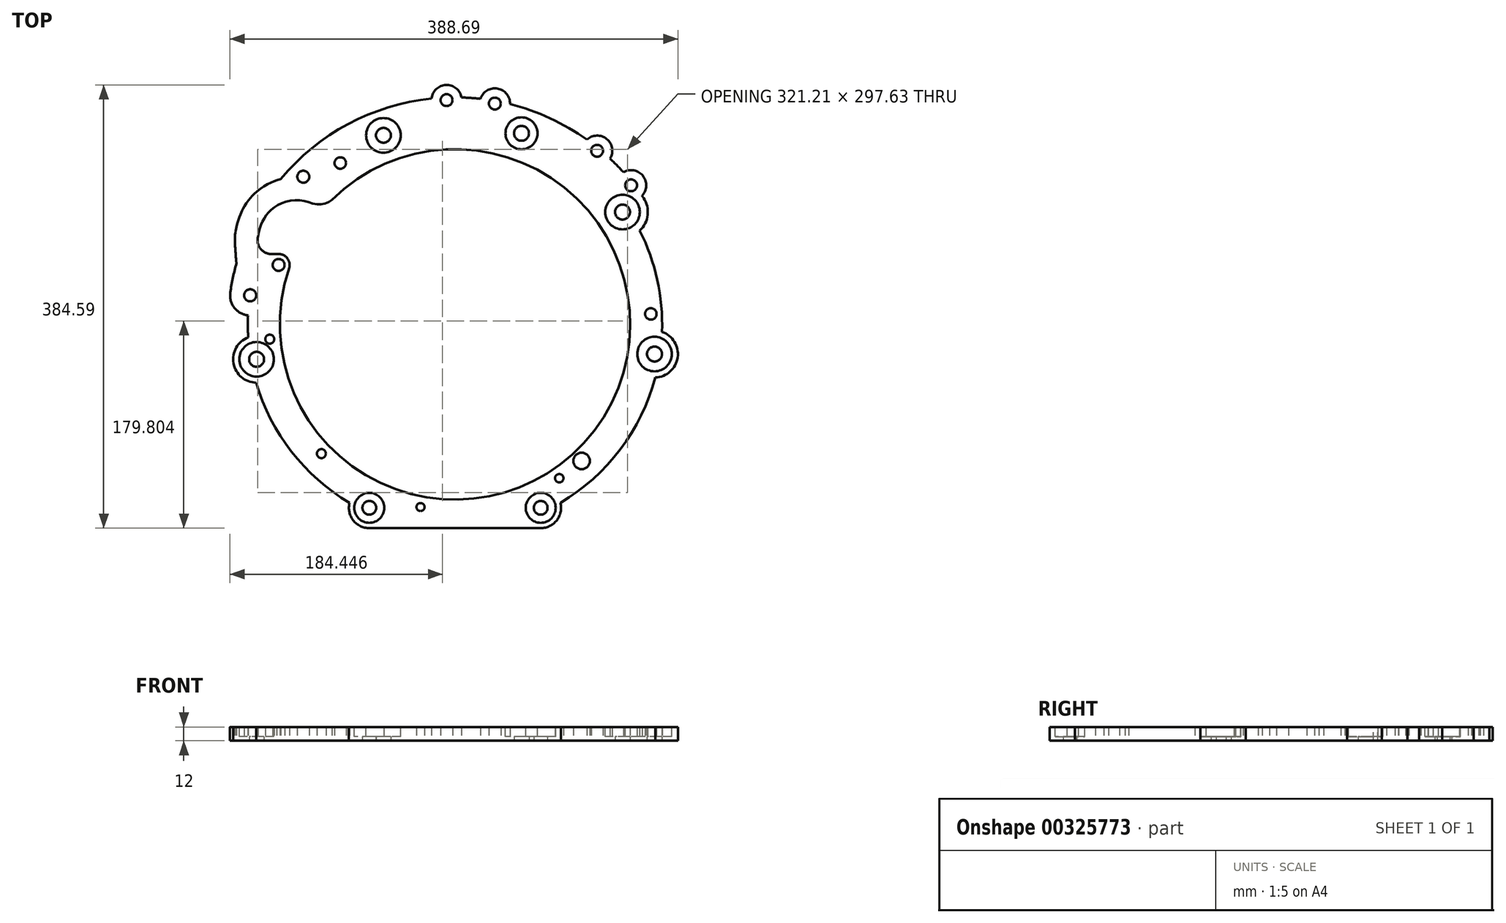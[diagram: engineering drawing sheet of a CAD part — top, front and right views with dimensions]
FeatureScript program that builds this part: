
annotation { "Feature Type Name" : "Feature", "Feature Type Description" : "" }
export const myFeature = defineFeature(function(context is Context, id is Id, definition is map)
    precondition{}
    {
        {
            var Q0;
            Q0=qCreatedBy(makeId("Top.planeOp"),FACE);
            var sketch = newSketch(context, id + "F0", { "sketchPlane" : qUnion([Q0])});
            skArc(sketch, "E0", {"start": v(-144.04, 48.53) * mm, "mid": v(128.94, -80.48) * mm, "end": v(-106.87, 108.08) * mm});
            skCircle(sketch, "E1", {"center": v(-74.38, -159.15) * mm, "radius": 5.97 * mm});
            skCircle(sketch, "E2.MirrorC", {"center": v(74.38, -159.15) * mm, "radius": 5.97 * mm});
            skCircle(sketch, "E3", {"center": v(-172.21, -30.27) * mm, "radius": 6.5 * mm});
            skCircle(sketch, "E4", {"center": v(173.17, -25.74) * mm, "radius": 6.47 * mm});
            skLineSegment(sketch, "E5", {"start": v(-74.38, -176.83) * mm, "end": v(74.47, -176.83) * mm});
            skCircle(sketch, "E6", {"center": v(-177.7, 25.2) * mm, "radius": 5.25 * mm});
            skCircle(sketch, "E7", {"center": v(-131.66, 128.11) * mm, "radius": 5.22 * mm});
            skCircle(sketch, "E8", {"center": v(-153.1, 51.58) * mm, "radius": 5.2 * mm});
            skArc(sketch, "E9", {"start": v(-144.04, 48.53) * mm, "mid": v(-145.8, 57.76) * mm, "end": v(-154.62, 61) * mm});
            skArc(sketch, "E10", {"start": v(-171.05, 75.95) * mm, "mid": v(-168.87, 65.79) * mm, "end": v(-159.58, 61.1) * mm});
            skLineSegment(sketch, "E11", {"start": v(-154.62, 61) * mm, "end": v(-159.58, 61.1) * mm});
            skFitSpline(sketch, "E12", {"points": [v(-106.87, 108.08) * mm, v(-118.68, 104.21) * mm, v(-133.94, 107.62) * mm, v(-150.31, 105.35) * mm, v(-161.48, 97.6) * mm, v(-167.29, 88.8) * mm, v(-171.05, 75.95) * mm], "startDerivative": vector(-61.8, -51.8) * mm, "endDerivative": vector(-19.09, -108) * mm});
            skCircle(sketch, "E13", {"center": v(-62.14, 164.08) * mm, "radius": 6.45 * mm});
            skCircle(sketch, "E14", {"center": v(57.71, 165.82) * mm, "radius": 6.47 * mm});
            skCircle(sketch, "E15", {"center": v(145.43, 97.48) * mm, "radius": 6.47 * mm});
            skCircle(sketch, "E16", {"center": v(-153.1, 51.58) * mm, "radius": 7.15 * mm, "construction": true});
            skCircle(sketch, "E17", {"center": v(-62.14, 164.08) * mm, "radius": 14.9 * mm, "construction": true});
            skArc(sketch, "E18", {"start": v(-189.68, 53.22) * mm, "mid": v(-192.79, 40.53) * mm, "end": v(-195.05, 27.67) * mm});
            skCircle(sketch, "E19", {"center": v(-99.57, 140) * mm, "radius": 5 * mm});
            skCircle(sketch, "E20", {"center": v(169.96, 9.12) * mm, "radius": 5 * mm});
            skFitSpline(sketch, "E21", {"points": [v(-190.74, 79.43) * mm, v(-190.74, 66.14) * mm, v(-189.68, 53.22) * mm], "startDerivative": vector(-3.85, -38.63) * mm, "endDerivative": vector(4.36, -49.57) * mm});
            skFitSpline(sketch, "E22.trimOffspring", {"points": [v(-116.71, 124.1) * mm, v(-116.76, 124.1) * mm, v(-116.85, 124.1) * mm, v(-116.98, 124.12) * mm, v(-117.1, 124.14) * mm, v(-117.18, 124.15) * mm, v(-117.24, 124.15) * mm, v(-117.28, 124.16) * mm, v(-117.32, 124.16) * mm, v(-117.35, 124.17) * mm, v(-117.37, 124.17) * mm, v(-117.38, 124.17) * mm, v(-117.4, 124.17) * mm, v(-117.4, 124.17) * mm, v(-117.4, 124.17) * mm, v(-117.4, 124.17) * mm, v(-117.4, 124.17) * mm, v(-117.4, 124.17) * mm, v(-117.4, 124.17) * mm, v(-117.4, 124.17) * mm, v(-117.42, 124.17) * mm, v(-117.44, 124.18) * mm, v(-117.48, 124.18) * mm, v(-117.57, 124.2) * mm, v(-117.73, 124.23) * mm, v(-117.93, 124.27) * mm, v(-118.18, 124.32) * mm, v(-118.56, 124.42) * mm, v(-119.16, 124.57) * mm, v(-120.03, 124.8) * mm, v(-121.05, 125.1) * mm, v(-122.23, 125.44) * mm, v(-123.55, 125.8) * mm, v(-125.02, 126.2) * mm, v(-126.63, 126.6) * mm, v(-128.1, 126.9) * mm, v(-129.37, 127.14) * mm, v(-130.19, 127.28) * mm, v(-130.86, 127.38) * mm, v(-131.55, 127.48) * mm, v(-132.41, 127.59) * mm, v(-133.44, 127.69) * mm, v(-134.8, 127.8) * mm, v(-137.17, 127.9) * mm, v(-140.5, 127.86) * mm, v(-144.39, 127.5) * mm, v(-148.18, 126.87) * mm, v(-151.87, 125.98) * mm, v(-154.86, 125.03) * mm, v(-157.2, 124.16) * mm, v(-159.5, 123.2) * mm, v(-162.26, 121.87) * mm, v(-166.44, 119.48) * mm, v(-170.23, 116.76) * mm, v(-173.22, 114.14) * mm, v(-174.83, 112.58) * mm, v(-175.99, 111.37) * mm, v(-177.1, 110.15) * mm, v(-178.5, 108.5) * mm, v(-180.1, 106.4) * mm, v(-181.8, 103.89) * mm, v(-183.05, 101.81) * mm, v(-183.95, 100.17) * mm, v(-184.58, 98.96) * mm, v(-185.08, 97.96) * mm, v(-185.45, 97.17) * mm, v(-185.82, 96.37) * mm, v(-186.27, 95.34) * mm, v(-186.98, 93.64) * mm, v(-187.8, 91.4) * mm, v(-188.7, 88.6) * mm, v(-189.46, 85.7) * mm, v(-190.14, 82.67) * mm, v(-190.55, 80.54) * mm, v(-190.74, 79.43) * mm]});
            skArc(sketch, "E23", {"start": v(-91.5, -154.78) * mm, "mid": v(-88.34, -170) * mm, "end": v(-74.38, -176.83) * mm});
            skArc(sketch, "E24", {"start": v(74.28, -176.83) * mm, "mid": v(88.3, -170.03) * mm, "end": v(91.5, -154.78) * mm});
            skArc(sketch, "E25", {"start": v(-195.05, 27.67) * mm, "mid": v(-191.54, 14.47) * mm, "end": v(-179.63, 7.8) * mm});
            skArc(sketch, "E26", {"start": v(160.32, 81.4) * mm, "mid": v(167.2, 94.93) * mm, "end": v(163.64, 109.7) * mm});
            skArc(sketch, "E27.trimOffspring", {"start": v(163.64, 109.7) * mm, "mid": v(162.98, 110.66) * mm, "end": v(162.32, 111.63) * mm});
            skArc(sketch, "E28", {"start": v(-179.63, 7.8) * mm, "mid": v(-179.8, -1.75) * mm, "end": v(-179.44, -11.3) * mm});
            skArc(sketch, "E29.trimOffspring", {"start": v(179.68, -6.52) * mm, "mid": v(175.6, 38.67) * mm, "end": v(160.32, 81.4) * mm});
            skArc(sketch, "E30.trimOffspring", {"start": v(91.5, -154.78) * mm, "mid": v(143.36, -108.51) * mm, "end": v(173.8, -46.03) * mm});
            skArc(sketch, "E31.trimOffspring", {"start": v(-172.54, -50.56) * mm, "mid": v(-141.93, -110.38) * mm, "end": v(-91.5, -154.78) * mm});
            skArc(sketch, "E32", {"start": v(-179.44, -11.3) * mm, "mid": v(-192.2, -33.78) * mm, "end": v(-172.54, -50.56) * mm});
            skArc(sketch, "E33", {"start": v(173.8, -46.03) * mm, "mid": v(193.25, -28.73) * mm, "end": v(179.68, -6.52) * mm});
            skCircle(sketch, "E34", {"center": v(-172.21, -30.27) * mm, "radius": 14.9 * mm, "construction": true});
            skCircle(sketch, "E35", {"center": v(90.5, -133.51) * mm, "radius": 3.65 * mm});
            skCircle(sketch, "E36", {"center": v(-29.93, -158.5) * mm, "radius": 3.5 * mm});
            skCircle(sketch, "E37", {"center": v(-115.93, -112.15) * mm, "radius": 3.9 * mm});
            skCircle(sketch, "E38", {"center": v(-160.8, -12.8) * mm, "radius": 3.91 * mm});
            skCircle(sketch, "E39", {"center": v(109.87, -118.5) * mm, "radius": 7.2 * mm});
            skCircle(sketch, "E40", {"center": v(173.17, -25.74) * mm, "radius": 14.9 * mm, "construction": true});
            skCircle(sketch, "E41", {"center": v(-7.32, 194.61) * mm, "radius": 5.15 * mm});
            skCircle(sketch, "E42", {"center": v(34.58, 191.66) * mm, "radius": 5.15 * mm});
            skCircle(sketch, "E43", {"center": v(123.38, 150.68) * mm, "radius": 5.15 * mm});
            skCircle(sketch, "E44", {"center": v(152.82, 120.72) * mm, "radius": 5.15 * mm});
            skCircle(sketch, "E45", {"center": v(145.43, 97.48) * mm, "radius": 14.9 * mm, "construction": true});
            skCircle(sketch, "E46", {"center": v(57.71, 165.82) * mm, "radius": 14.9 * mm, "construction": true});
            skArc(sketch, "E47", {"start": v(5.63, 196.92) * mm, "mid": v(-7.81, 207.75) * mm, "end": v(-20.4, 195.94) * mm});
            skArc(sketch, "E48", {"start": v(47.72, 191.13) * mm, "mid": v(36.91, 204.6) * mm, "end": v(22.08, 195.76) * mm});
            skArc(sketch, "E49", {"start": v(134.6, 143.84) * mm, "mid": v(131.71, 160.86) * mm, "end": v(114.46, 160.34) * mm});
            skArc(sketch, "E50.trimOffspring", {"start": v(162.32, 111.63) * mm, "mid": v(163.14, 128.88) * mm, "end": v(146.17, 132.07) * mm});
            skArc(sketch, "E51.trimOffspring", {"start": v(-20.4, 195.94) * mm, "mid": v(-92.73, 173.81) * mm, "end": v(-151.38, 126.07) * mm});
            skArc(sketch, "E52.trimOffspring", {"start": v(22.08, 195.76) * mm, "mid": v(13.87, 196.51) * mm, "end": v(5.63, 196.92) * mm});
            skArc(sketch, "E53.trimOffspring", {"start": v(114.46, 160.34) * mm, "mid": v(82.54, 178.88) * mm, "end": v(47.72, 191.13) * mm});
            skArc(sketch, "E54.trimOffspring", {"start": v(146.17, 132.07) * mm, "mid": v(140.51, 138.08) * mm, "end": v(134.6, 143.84) * mm});
            skSolve(sketch);
        }
        {
            var Q0;
            Q0=makeQuery(id+"F0.imprint","IMPRINT",FACE,{"disambiguationData":[TD([[makeQuery(id+"F0.imprint","IMPRINT",EDGE,{"derivedFrom":sQuery(id+"F0.wireOp",EDGE,"E0")}),-1.0]])]});
            var Q1;
            Q1=makeQuery(id+"F0.imprint","IMPRINT",FACE,{"disambiguationData":[TD([[makeQuery(id+"F0.imprint","IMPRINT",EDGE,{"derivedFrom":sQuery(id+"F0.wireOp",EDGE,"E3")}),-1.0]])]});
            var Q2;
            Q2=makeQuery(id+"F0.imprint","IMPRINT",FACE,{"disambiguationData":[TD([[makeQuery(id+"F0.imprint","IMPRINT",EDGE,{"derivedFrom":sQuery(id+"F0.wireOp",EDGE,"E4")}),-1.0]])]});
            var Q3;
            Q3=makeQuery(id+"F0.imprint","IMPRINT",FACE,{"disambiguationData":[TD([[makeQuery(id+"F0.imprint","IMPRINT",EDGE,{"derivedFrom":sQuery(id+"F0.wireOp",EDGE,"E13")}),-1.0]])]});
            var Q4;
            Q4=makeQuery(id+"F0.imprint","IMPRINT",FACE,{"disambiguationData":[TD([[makeQuery(id+"F0.imprint","IMPRINT",EDGE,{"derivedFrom":sQuery(id+"F0.wireOp",EDGE,"E7")}),-1.0]])]});
            var Q5;
            Q5=makeQuery(id+"F0.imprint","IMPRINT",FACE,{"disambiguationData":[TD([[makeQuery(id+"F0.imprint","IMPRINT",EDGE,{"derivedFrom":sQuery(id+"F0.wireOp",EDGE,"E8")}),-1.0]])]});
            extrude(context, id + "F1", {"entities" : qUnion([Q0, Q1, Q2, Q3, Q4, Q5]), "depth" : 12 * mm});
        }
        {
            var Q0;
            Q0=makeQuery(id+"F1.opExtrude","CAP_FACE",FACE,{"disambiguationData":[OSD([sQuery(id+"F0.wireOp",EDGE,"E0"),sQuery(id+"F0.wireOp",EDGE,"E1"),sQuery(id+"F0.wireOp",EDGE,"E2.MirrorC"),sQuery(id+"F0.wireOp",EDGE,"E3"),sQuery(id+"F0.wireOp",EDGE,"E4"),sQuery(id+"F0.wireOp",EDGE,"E5"),sQuery(id+"F0.wireOp",EDGE,"E6"),sQuery(id+"F0.wireOp",EDGE,"E7"),sQuery(id+"F0.wireOp",EDGE,"E8"),sQuery(id+"F0.wireOp",EDGE,"E9"),sQuery(id+"F0.wireOp",EDGE,"E10"),sQuery(id+"F0.wireOp",EDGE,"E11"),sQuery(id+"F0.wireOp",EDGE,"E12"),sQuery(id+"F0.wireOp",EDGE,"E13"),sQuery(id+"F0.wireOp",EDGE,"E14"),sQuery(id+"F0.wireOp",EDGE,"E15"),sQuery(id+"F0.wireOp",EDGE,"ERYoM1TZ-LeGq-j3Lg-Inw0-2qhC6B0PDWU5"),sQuery(id+"F0.wireOp",EDGE,"E18"),sQuery(id+"F0.wireOp",EDGE,"E19"),sQuery(id+"F0.wireOp",EDGE,"E20"),sQuery(id+"F0.wireOp",EDGE,"MDjsRgp3-xdrw-438o-E8S3-B8phiH2VUBZX"),sQuery(id+"F0.wireOp",EDGE,"E21"),sQuery(id+"F0.wireOp",EDGE,"E22.trimOffspring"),sQuery(id+"F0.wireOp",EDGE,"E23"),sQuery(id+"F0.wireOp",EDGE,"E24"),sQuery(id+"F0.wireOp",EDGE,"E25"),sQuery(id+"F0.wireOp",EDGE,"E26"),sQuery(id+"F0.wireOp",EDGE,"E27.trimOffspring"),sQuery(id+"F0.wireOp",EDGE,"E28"),sQuery(id+"F0.wireOp",EDGE,"E29.trimOffspring"),sQuery(id+"F0.wireOp",EDGE,"E30.trimOffspring"),sQuery(id+"F0.wireOp",EDGE,"E31.trimOffspring")])],"isStart":false});
            var sketch = newSketch(context, id + "F2", { "sketchPlane" : qUnion([Q0])});
            skCircle(sketch, "E55", {"center": v(-62.14, 164.08) * mm, "radius": 15 * mm});
            skCircle(sketch, "E56", {"center": v(57.71, 165.82) * mm, "radius": 13.86 * mm});
            skCircle(sketch, "E57", {"center": v(145.43, 97.48) * mm, "radius": 15 * mm});
            skCircle(sketch, "E58", {"center": v(-172.21, -30.27) * mm, "radius": 15 * mm});
            skCircle(sketch, "E59", {"center": v(173.17, -25.74) * mm, "radius": 15 * mm});
            skCircle(sketch, "E60", {"center": v(-74.38, -159.15) * mm, "radius": 13 * mm});
            skCircle(sketch, "E61", {"center": v(74.38, -159.15) * mm, "radius": 13 * mm});
            skSolve(sketch);
        }
        {
            var Q0;
            Q0 = qSketchRegion(id + "F2", true);
            extrude(context, id + "F3", {"entities" : qUnion([Q0]), "operationType" : NewBodyOperationType.REMOVE, "oppositeDirection" : true, "depth" : 8.5 * mm});
        }
    });
